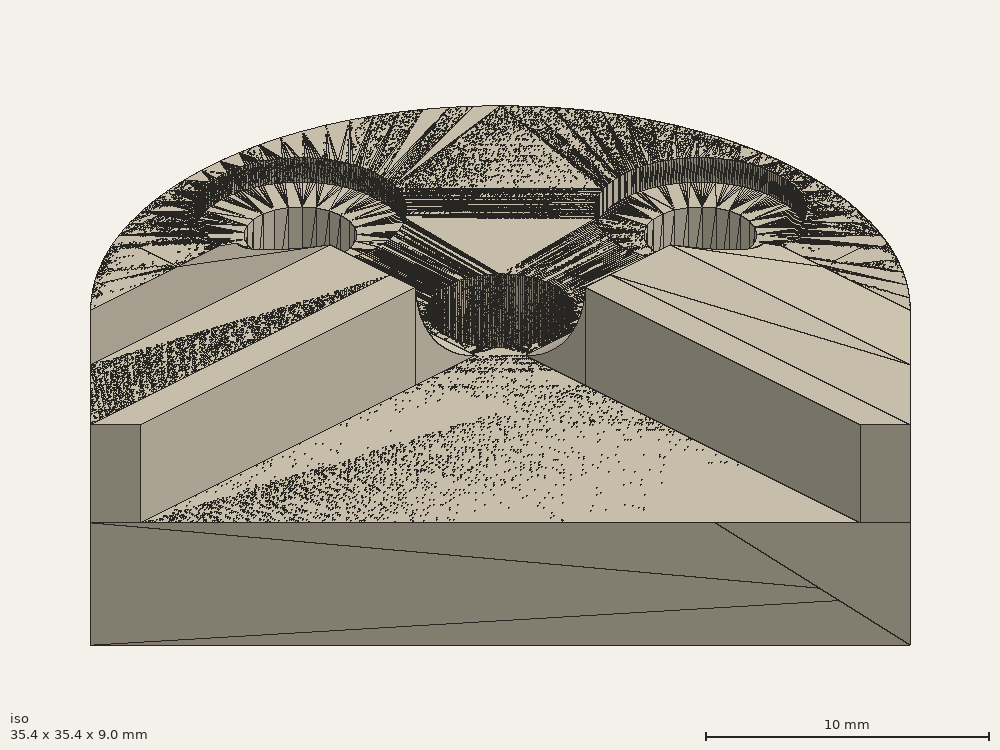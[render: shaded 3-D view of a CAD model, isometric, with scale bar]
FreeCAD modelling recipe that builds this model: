
FCSTD DOCUMENT  (FreeCAD 0.17R11850 (Git))
Label: bed_corner_mini_2pb_foxglove_v2
License: All rights reserved
LicenseURL: http://en.wikipedia.org/wiki/All_rights_reserved
objects: PartDesign::Pocket×8, PartDesign::Pad×6, Sketcher::SketchObject×5, Part::Feature×3, Mesh::Feature×1, PartDesign::Body×1
note: 37 computed .brp shape members not serialized (recipe doc carries the construction recipe); baked Part::Feature solids carry a one-line shape summary decoded from their .brp

FEATURE [Mesh::Feature] bed_corner_mini_2pb_foxglove
FEATURE [Part::Feature] bed_corner_mini_2pb_foxglove001
  shape: bbox 35.35 x 35.35 x 9 mm, 3154 faces, 0 solids (baked)
FEATURE [Part::Feature] bed_corner_mini_2pb_foxglove001_solid  label="bed_corner_mini_2pb_foxglove001 (Solid)"
  shape: bbox 35.35 x 35.35 x 9 mm, 3154 faces (baked)
FEATURE [Part::Feature] bed_corner_mini_2pb_foxglove001_solid001  label="bed_corner_mini_2pb_foxglove001 (Solid)001"
  shape: bbox 35.35 x 35.35 x 9 mm, 797 faces (baked)
FEATURE [PartDesign::Pad] Pad
  BaseFeature = -> bed_corner_mini_2pb_foxglove001_solid001
  Length = 1.25
  Length2 = 100
  Profile = -> bed_corner_mini_2pb_foxglove001_solid001 [Face786]
  Type = 0
FEATURE [PartDesign::Pad] Pad001
  BaseFeature = -> Pad
  Length = 1.25
  Length2 = 100
  Profile = -> Pad [Face313]
  Type = 0
FEATURE [PartDesign::Pocket] Pocket
  BaseFeature = -> Pad001
  Length = 5
  Profile = -> Pad001 [Face308]
  Type = 1
FEATURE [PartDesign::Pocket] Pocket001
  BaseFeature = -> Pocket
  Length = 5
  Profile = -> Pocket [Face311]
  Type = 1
FEATURE [Sketcher::SketchObject] Sketch
  ExternalGeometry = -> [Pocket001]
  MapMode = 5
  Placement = pos=(-5.85962,0,0) rot=(0.57735,0.57735,0.57735;2.0944rad)
  Support = -> [Pocket001]
  sketch-geometry (3):
    g0: LineSegment StartX=2.64648 StartY=7 StartZ=0 EndX=10.2531 EndY=3 EndZ=0
    g1: LineSegment StartX=2.64648 StartY=7 StartZ=0 EndX=2.64648 EndY=3 EndZ=0
    g2: LineSegment StartX=2.64648 StartY=3 StartZ=0 EndX=10.2531 EndY=3 EndZ=0
  constraints (7):
    c: Coincident(g0,g-3)
    c: Coincident(g0,g-4)
    c: Coincident(g1,g0)
    c: Vertical(g1)
    c: Coincident(g2,g1)
    c: Coincident(g2,g0)
    c: Horizontal(g2)
FEATURE [PartDesign::Pad] Pad002
  BaseFeature = -> Pocket001
  Length = 15
  Length2 = 100
  Profile = -> Sketch
  Reversed = true
  Type = 0
FEATURE [PartDesign::Pocket] Pocket002
  BaseFeature = -> Pad002
  Length = 5
  Profile = -> Pad002 [Face313]
  Type = 1
FEATURE [Sketcher::SketchObject] Sketch001
  ExternalGeometry = -> [Pocket002]
  MapMode = 5
  Placement = pos=(0,-5.85962,0) rot=(0,0.707107,0.707107;3.14159rad)
  Support = -> [Pocket002]
  sketch-geometry (3):
    g0: LineSegment StartX=-2.64649 StartY=7 StartZ=0 EndX=-2.64649 EndY=3 EndZ=0
    g1: LineSegment StartX=-10.2531 StartY=3 StartZ=0 EndX=-2.64649 EndY=7 EndZ=0
    g2: LineSegment StartX=-10.2531 StartY=3 StartZ=0 EndX=-2.64649 EndY=3 EndZ=0
  constraints (7):
    c: Coincident(g0,g-3)
    c: Vertical(g0)
    c: Coincident(g1,g-4)
    c: Coincident(g1,g0)
    c: Coincident(g2,g1)
    c: Coincident(g2,g0)
    c: Horizontal(g2)
FEATURE [PartDesign::Pad] Pad003
  BaseFeature = -> Pocket002
  Length = 15
  Length2 = 100
  Profile = -> Sketch001
  Reversed = true
  Type = 0
FEATURE [PartDesign::Pocket] Pocket003
  BaseFeature = -> Pad003
  Length = 5
  Profile = -> Pad003 [Face319]
  Type = 1
FEATURE [Sketcher::SketchObject] Sketch002
  ExternalGeometry = -> [Pocket003]
  MapMode = 5
  Placement = pos=(-1.60351,0,0) rot=(0.57735,-0.57735,-0.57735;2.0944rad)
  Support = -> [Pocket003]
  sketch-geometry (4):
    g0: GeomPoint X=2.85962 Y=3 Z=0
    g1: ArcOfCircle CenterX=1.3663 CenterY=7.24499 CenterZ=0 NormalX=0 NormalY=0 NormalZ=1 Radius=4.5 StartAngle=5.05065 EndAngle=6.22872
    g2: LineSegment StartX=2.85962 StartY=3 StartZ=0 EndX=5.85962 EndY=3 EndZ=0
    g3: LineSegment StartX=5.85962 StartY=7 StartZ=0 EndX=5.85962 EndY=3 EndZ=0
  constraints (9):
    c: DistanceY(g-4,g0) = 0
    c: DistanceX(g0,g-4) = 3
    c: Coincident(g1,g0)
    c: Coincident(g1,g-4)
    c: Radius(g1) = 4.5
    c: Coincident(g2,g0)
    c: Coincident(g2,g-4)
    c: Coincident(g3,g1)
    c: Coincident(g3,g2)
FEATURE [PartDesign::Pad] Pad004
  BaseFeature = -> Pocket003
  Length = 15
  Length2 = 100
  Profile = -> Sketch002
  Reversed = true
  Type = 0
FEATURE [Sketcher::SketchObject] Sketch003
  ExternalGeometry = -> [Pad004]
  MapMode = 5
  Placement = pos=(0,0,2) rot=(0,0,1;0rad)
  Support = -> [Pad004]
  sketch-geometry (2):
    g0: Circle [constr] CenterX=10 CenterY=8.8294e-08 CenterZ=0 NormalX=0 NormalY=0 NormalZ=1 Radius=2
    g1: Circle CenterX=10 CenterY=8.8294e-08 CenterZ=0 NormalX=0 NormalY=0 NormalZ=1 Radius=3.75288
  constraints (5):
    c: PointOnObject(g-6,g0)
    c: PointOnObject(g-4,g0)
    c: PointOnObject(g-7,g0)
    c: Coincident(g1,g0)
    c: PointOnObject(g-10,g1)
FEATURE [PartDesign::Pocket] Pocket004
  BaseFeature = -> Pad004
  Length = 5
  Profile = -> Sketch003
  Reversed = true
  Type = 0
FEATURE [PartDesign::Pocket] Pocket005
  BaseFeature = -> Pocket004
  Length = 5
  Profile = -> Pocket004 [Face656]
  Type = 0
FEATURE [Sketcher::SketchObject] Sketch004
  ExternalGeometry = -> [Pocket005]
  MapMode = 5
  Placement = pos=(1.04816e-06,-1.60352,0) rot=(1,0,0;1.5708rad)
  Support = -> [Pocket005]
  sketch-geometry (4):
    g0: GeomPoint X=-2.85962 Y=3 Z=0
    g1: ArcOfCircle CenterX=-1.36629 CenterY=7.24499 CenterZ=0 NormalX=0 NormalY=0 NormalZ=1 Radius=4.5 StartAngle=3.19606 EndAngle=4.37412
    g2: LineSegment StartX=-5.85962 StartY=7 StartZ=0 EndX=-5.85962 EndY=3 EndZ=0
    g3: LineSegment StartX=-5.85962 StartY=3 StartZ=0 EndX=-2.85962 EndY=3 EndZ=0
  constraints (9):
    c: DistanceY(g-3,g0) = 0
    c: DistanceX(g-3,g0) = 3
    c: Coincident(g1,g-3)
    c: Coincident(g1,g0)
    c: Radius(g1) = 4.5
    c: Coincident(g2,g1)
    c: Coincident(g2,g-3)
    c: Coincident(g3,g2)
    c: Coincident(g3,g0)
FEATURE [PartDesign::Pad] Pad005
  BaseFeature = -> Pocket005
  Length = 15
  Length2 = 100
  Profile = -> Sketch004
  Reversed = true
  Type = 0
FEATURE [PartDesign::Pocket] Pocket006
  BaseFeature = -> Pad005
  Length = 5
  Profile = -> Pad005 [Face670]
  Type = 0
FEATURE [PartDesign::Pocket] Pocket007
  BaseFeature = -> Pocket006
  Length = 5
  Profile = -> Pocket006 [Face605]
  Type = 0
FEATURE [PartDesign::Body] Body
  BaseFeature = -> bed_corner_mini_2pb_foxglove001_solid001
  Group = -> [Pad,Pad001,Pocket,Pocket001,Sketch,Pad002,Pocket002,Sketch001,Pad003,Pocket003,Sketch002,Pad004,Sketch003,Pocket004,Pocket005,Sketch004,Pad005,Pocket006,Pocket007]
  Origin = -> Origin
  Tip = -> Pocket007
